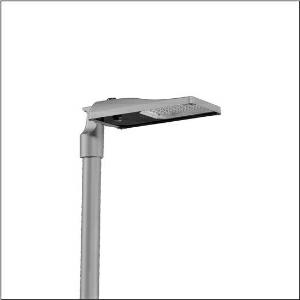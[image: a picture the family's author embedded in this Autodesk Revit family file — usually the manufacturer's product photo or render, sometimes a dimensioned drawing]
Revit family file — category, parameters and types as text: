
# Revit family: streetlight_sl_31_mini___st0_8a_5xh6c31t08ha_0974
name_source: partatom
category: Lighting Fixtures
units: mm (PartAtom-declared; Revit-internal decimal feet)

## family parameters
Cut with Voids When Loaded = No
Host = Face
Light Source = No
Part Type = Normal
Room Calculation Point = No
Round Connector Dimension = Use Diameter
Shared = No

## types (1)
- --- (1 x LED, 9230 lm, 68.3 W, 3000K)
    Apparent Load = 68 VA
    CIE Flux Codes = 38 75 97 100 100
    Color Rendering = 70
    Color Temperature = 3000K
    Default Elevation = 1800 mm
    Description = Streetlight SL 31 mini D4i, Desk-Remote mast luminaire for post-top, side-entry; light control with lens of PMMA; light distribution: ST0.8a, direct asymmetric distribution, for standard-compliant lighting for roads and squares; LED: luminous flux: 9.230lm, light colour: 730, colour temperature: 3000K; luminous efficacy: 135,3lm/W; control: pre-setting: logarithmic dimming characteristic, flexible luminous flux parameterisation, time-dependent luminous flux control, constant luminous flux control, power reduction, intelligent temperature release in ECG and LED module, overheat protection; luminaire housing, of diecast aluminium, Siteco® metallic grey (DB 702S), corrosivity category C5 high according to DIN EN ISO 12944; cover of toughened safety glass, transparent, opened without tools; mast flange of diecast aluminium, Siteco® metallic grey (DB 702S), spigot size: 76/60mm, mast flange included unmounted; with cable H07RN-F 2x 1.5mm², cable length: 8,5m, connection cable pre-assembled; mains connection: 220..240V, AC, 50/60Hz; power consumption (at start of service life): 68,2W / (at end of service life): 74,4W / (with reduced operation 50%): 29,7W; protection rating (complete): IP66; insulation class (complete): insulation class II (safety insulation); impact resistance: IK09; certification: CE, ENEC, ENEC+, VDE, UKCA, ZD4i; permissible operating ambient temperature for outdoor applications: -40..+50°C; packaging unit: 1 piece

Light Distribution: ST0.8a
    Height = 76 mm
    Lamp = 1 x LED
    Lamp Light Flux = 9230 lm
    Lamp Power = 68.3 W
    Lamp count = 1
    Length = 547 mm
    Luminous efficacy = 135 lm/W
    Manufacturer = Siteco
    ModVariant = No
    Model = 5XH6C31T08HA
    Number of Poles = 1
    OnlyDefault = Yes
    Power Factor = 1
    Product Name = Streetlight SL 31 mini | ST0.8a
    Product group = mast luminaire | pylon top
    ProductGroupID = 6100
    Protection Class = Protection class II
    Protection Degree = IP 66
    RLX_Detail_Level = 1
    RLX_Emergency_Light_Flux = 0 lm
    RLX_Emergency_Type = 0
    RLX_Emergency_Type_DB = No
    RlxData = <blob elided: 24357 chars, md5=564f00e3>
    Socket = socket
    Standby Power = 0 W
    System Light Flux = 9230 lm
    System Power = 68 W
    Type Comments = factory setting: luminous flux: 100 % | dim-lin: 254 | 692 mA
    Type Image = l_1300332.jpg
    URL = http://relux.com
    VarID = @adj_002235
    Voltage = 0 V
    Weight = 0.00 kg
    Width = 265 mm

## geometry (parser evidence)
native form markers: Blend x4, Sweep x10
no freeform markers — native parametric forms only
